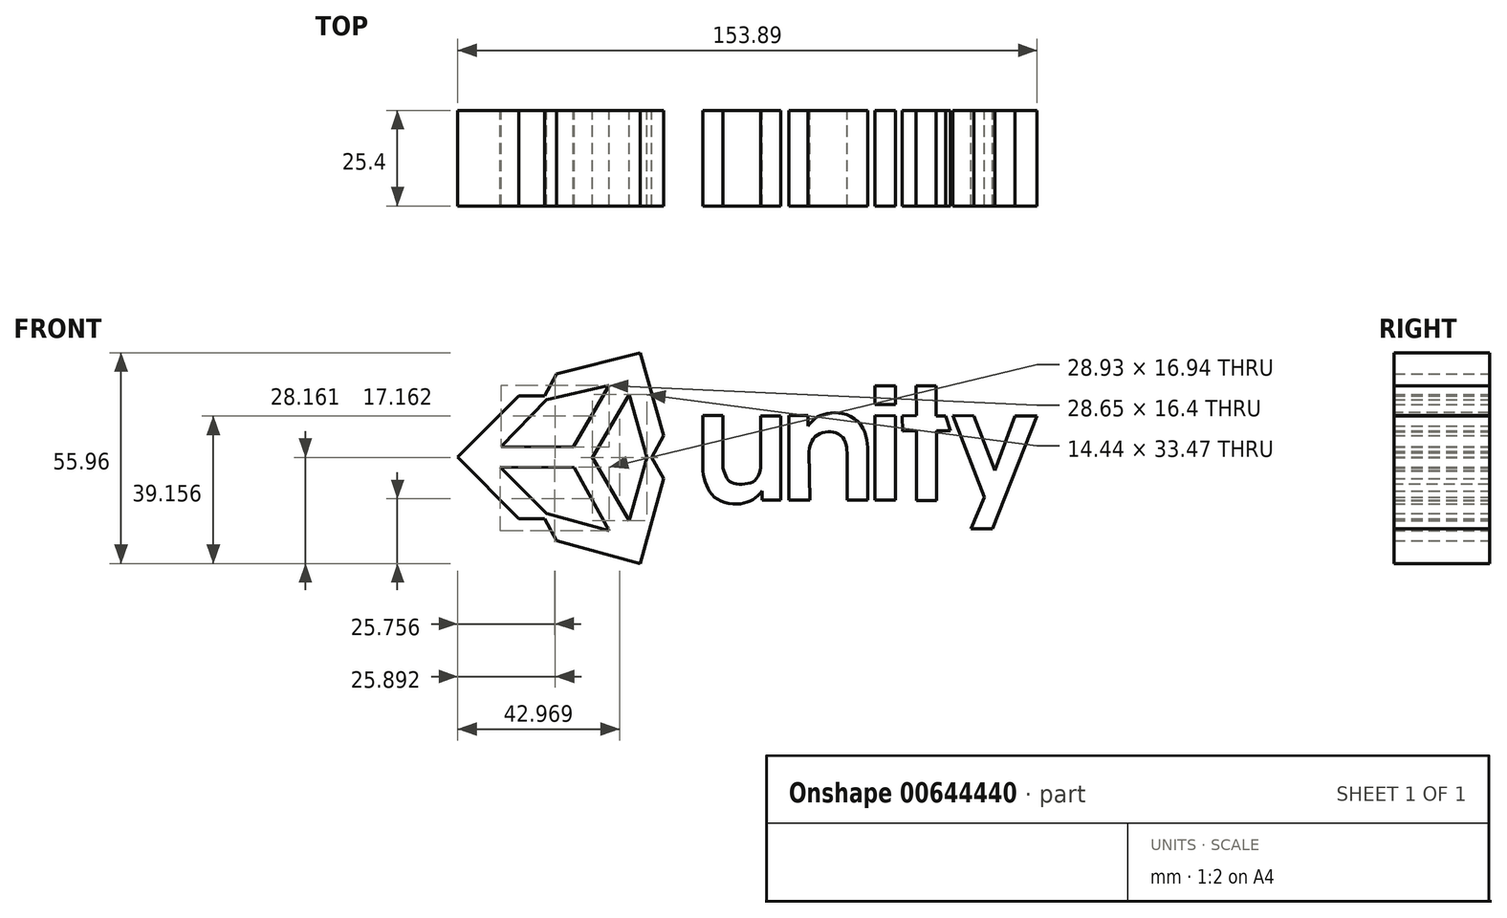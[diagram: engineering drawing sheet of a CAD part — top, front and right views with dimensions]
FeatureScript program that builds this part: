
annotation { "Feature Type Name" : "Feature", "Feature Type Description" : "" }
export const myFeature = defineFeature(function(context is Context, id is Id, definition is map)
    precondition{}
    {
        {
            var Q0;
            Q0=qCreatedBy(makeId("Front.planeOp"),FACE);
            var sketch = newSketch(context, id + "F0", { "sketchPlane" : qUnion([Q0])});
            skLineSegment(sketch, "E0", {"start": v(-78.08, -6.27) * mm, "end": v(-61.82, 10) * mm});
            skLineSegment(sketch, "E1", {"start": v(-61.82, 10) * mm, "end": v(-54.99, 10) * mm});
            skLineSegment(sketch, "E2", {"start": v(-54.99, 10) * mm, "end": v(-51.78, 15.87) * mm});
            skLineSegment(sketch, "E3", {"start": v(-51.78, 15.87) * mm, "end": v(-29.6, 21.48) * mm});
            skLineSegment(sketch, "E4", {"start": v(-29.6, 21.48) * mm, "end": v(-23.43, -0.5) * mm});
            skLineSegment(sketch, "E5", {"start": v(-23.43, -0.5) * mm, "end": v(-26.59, -6.29) * mm});
            skLineSegment(sketch, "E6", {"start": v(-26.59, -6.29) * mm, "end": v(-23.43, -11.97) * mm});
            skLineSegment(sketch, "E7", {"start": v(-23.43, -11.97) * mm, "end": v(-29.6, -34.48) * mm});
            skLineSegment(sketch, "E8", {"start": v(-29.6, -34.48) * mm, "end": v(-51.78, -28.4) * mm});
            skLineSegment(sketch, "E9", {"start": v(-51.78, -28.4) * mm, "end": v(-54.99, -22.58) * mm});
            skLineSegment(sketch, "E10", {"start": v(-54.99, -22.58) * mm, "end": v(-61.93, -22.58) * mm});
            skLineSegment(sketch, "E11", {"start": v(-61.93, -22.58) * mm, "end": v(-78.08, -6.27) * mm});
            skLineSegment(sketch, "E12", {"start": v(-66.79, -8.85) * mm, "end": v(-54.55, -21.2) * mm});
            skLineSegment(sketch, "E13", {"start": v(-54.55, -21.2) * mm, "end": v(-37.86, -25.79) * mm});
            skLineSegment(sketch, "E14", {"start": v(-37.86, -25.79) * mm, "end": v(-47.13, -9) * mm});
            skLineSegment(sketch, "E15", {"start": v(-47.13, -9) * mm, "end": v(-66.79, -8.85) * mm});
            skLineSegment(sketch, "E16", {"start": v(-54.55, 9.05) * mm, "end": v(-66.51, -3.38) * mm});
            skLineSegment(sketch, "E17", {"start": v(-66.51, -3.38) * mm, "end": v(-47.39, -3.52) * mm});
            skLineSegment(sketch, "E18", {"start": v(-47.39, -3.52) * mm, "end": v(-37.86, 12.88) * mm});
            skLineSegment(sketch, "E19", {"start": v(-37.86, 12.88) * mm, "end": v(-54.55, 9.05) * mm});
            skLineSegment(sketch, "E20", {"start": v(-42.33, -6.29) * mm, "end": v(-32.5, -23.06) * mm});
            skLineSegment(sketch, "E21", {"start": v(-32.5, -23.06) * mm, "end": v(-27.9, -6.29) * mm});
            skLineSegment(sketch, "E22", {"start": v(-27.9, -6.29) * mm, "end": v(-32.5, 10.42) * mm});
            skLineSegment(sketch, "E23", {"start": v(-32.5, 10.42) * mm, "end": v(-42.33, -6.29) * mm});
            skLineSegment(sketch, "E24", {"start": v(-12.94, 4.77) * mm, "end": v(-12.94, -9.9) * mm});
            skLineSegment(sketch, "E25", {"start": v(-12.94, 4.77) * mm, "end": v(-7.58, 4.77) * mm});
            skLineSegment(sketch, "E26", {"start": v(-7.58, 4.77) * mm, "end": v(-7.58, -9.16) * mm});
            skLineSegment(sketch, "E27", {"start": v(2.4, -8.68) * mm, "end": v(2.4, 4.73) * mm});
            skLineSegment(sketch, "E28", {"start": v(2.4, 4.73) * mm, "end": v(7.76, 4.73) * mm});
            skLineSegment(sketch, "E29", {"start": v(7.76, 4.73) * mm, "end": v(7.76, -17.67) * mm});
            skLineSegment(sketch, "E30", {"start": v(7.76, -17.67) * mm, "end": v(2.75, -17.67) * mm});
            skLineSegment(sketch, "E31", {"start": v(2.75, -17.67) * mm, "end": v(2.75, -15.25) * mm});
            skLineSegment(sketch, "E32", {"start": v(14.94, 2.03) * mm, "end": v(14.94, 4.78) * mm});
            skLineSegment(sketch, "E33", {"start": v(14.94, 4.78) * mm, "end": v(9.91, 4.78) * mm});
            skLineSegment(sketch, "E34", {"start": v(9.91, 4.78) * mm, "end": v(9.91, -17.64) * mm});
            skLineSegment(sketch, "E35", {"start": v(9.91, -17.64) * mm, "end": v(15.46, -17.64) * mm});
            skLineSegment(sketch, "E36", {"start": v(15.22, -4.63) * mm, "end": v(15.46, -17.64) * mm});
            skLineSegment(sketch, "E37", {"start": v(25.34, -5.04) * mm, "end": v(25.34, -17.64) * mm});
            skLineSegment(sketch, "E38", {"start": v(25.34, -17.64) * mm, "end": v(30.8, -17.64) * mm});
            skLineSegment(sketch, "E39", {"start": v(30.8, -17.64) * mm, "end": v(30.8, -4.77) * mm});
            skLineSegment(sketch, "E40", {"start": v(32.8, 4.8) * mm, "end": v(32.8, -17.61) * mm});
            skLineSegment(sketch, "E41", {"start": v(32.8, -17.61) * mm, "end": v(38.16, -17.61) * mm});
            skLineSegment(sketch, "E42", {"start": v(38.16, -17.61) * mm, "end": v(38.16, 4.73) * mm});
            skLineSegment(sketch, "E43", {"start": v(38.16, 4.73) * mm, "end": v(32.8, 4.8) * mm});
            skLineSegment(sketch, "E44", {"start": v(32.8, 12.66) * mm, "end": v(32.8, 7.78) * mm});
            skLineSegment(sketch, "E45", {"start": v(32.8, 7.78) * mm, "end": v(38.17, 7.78) * mm});
            skLineSegment(sketch, "E46", {"start": v(38.17, 7.78) * mm, "end": v(38.17, 12.66) * mm});
            skLineSegment(sketch, "E47", {"start": v(38.17, 12.66) * mm, "end": v(32.8, 12.66) * mm});
            skLineSegment(sketch, "E48", {"start": v(43.7, 12.66) * mm, "end": v(43.84, 4.8) * mm});
            skLineSegment(sketch, "E49", {"start": v(43.84, 4.8) * mm, "end": v(40, 4.73) * mm});
            skLineSegment(sketch, "E50", {"start": v(40, 4.73) * mm, "end": v(40.08, 0.7) * mm});
            skLineSegment(sketch, "E51", {"start": v(40.08, 0.7) * mm, "end": v(43.83, 0.77) * mm});
            skLineSegment(sketch, "E52", {"start": v(43.83, 0.77) * mm, "end": v(43.83, -17.74) * mm});
            skLineSegment(sketch, "E53", {"start": v(43.83, -17.74) * mm, "end": v(49.16, -17.74) * mm});
            skLineSegment(sketch, "E54", {"start": v(49.16, -17.74) * mm, "end": v(49.16, 0.77) * mm});
            skLineSegment(sketch, "E55", {"start": v(49.16, 0.77) * mm, "end": v(52.85, 0.77) * mm});
            skLineSegment(sketch, "E56", {"start": v(52.85, 0.77) * mm, "end": v(51.48, 4.67) * mm});
            skLineSegment(sketch, "E57", {"start": v(51.48, 4.67) * mm, "end": v(49.02, 4.67) * mm});
            skLineSegment(sketch, "E58", {"start": v(49.02, 4.67) * mm, "end": v(49.02, 12.68) * mm});
            skLineSegment(sketch, "E59", {"start": v(49.02, 12.68) * mm, "end": v(43.7, 12.66) * mm});
            skLineSegment(sketch, "E60", {"start": v(53.4, 4.83) * mm, "end": v(61.8, -16.86) * mm});
            skLineSegment(sketch, "E61", {"start": v(61.8, -16.86) * mm, "end": v(58.21, -25.3) * mm});
            skLineSegment(sketch, "E62", {"start": v(58.21, -25.3) * mm, "end": v(64, -25.27) * mm});
            skLineSegment(sketch, "E63", {"start": v(64, -25.27) * mm, "end": v(75.81, 4.73) * mm});
            skLineSegment(sketch, "E64", {"start": v(75.81, 4.73) * mm, "end": v(70.02, 4.71) * mm});
            skLineSegment(sketch, "E65", {"start": v(70.02, 4.71) * mm, "end": v(64.64, -9.8) * mm});
            skLineSegment(sketch, "E66", {"start": v(64.64, -9.8) * mm, "end": v(59.06, 4.73) * mm});
            skLineSegment(sketch, "E67", {"start": v(59.06, 4.73) * mm, "end": v(53.4, 4.83) * mm});
            skFitSpline(sketch, "E68", {"points": [v(-7.58, -9.16) * mm, v(-6.3, -12.2) * mm, v(-4, -13.35) * mm, v(0, -12.93) * mm, v(1.9, -10.93) * mm, v(2.4, -8.68) * mm], "startDerivative": vector(4.25, -15.78) * mm, "endDerivative": vector(0, 7.44) * mm});
            skFitSpline(sketch, "E69", {"points": [v(-12.94, -9.9) * mm, v(-12, -13.8) * mm, v(-10, -16.74) * mm, v(-6, -18.52) * mm, v(-1.88, -18.41) * mm, v(0.86, -17.15) * mm, v(2.75, -15.25) * mm], "startDerivative": vector(2.04, -24.47) * mm, "endDerivative": vector(12.32, 14.15) * mm});
            skFitSpline(sketch, "E70", {"points": [v(14.94, 2.03) * mm, v(16.9, 4.05) * mm, v(19.73, 5.27) * mm, v(23.72, 5.44) * mm, v(28.02, 3.4) * mm, v(30.38, -0.65) * mm, v(30.8, -4.77) * mm], "startDerivative": vector(12.62, 15.54) * mm, "endDerivative": vector(0.48, -23.78) * mm});
            skFitSpline(sketch, "E71", {"points": [v(15.22, -4.63) * mm, v(15.75, -2.53) * mm, v(17.13, -0.58) * mm, v(19.5, 0.4) * mm, v(21.77, 0.4) * mm, v(23.96, -0.82) * mm, v(25.1, -2.93) * mm, v(25.34, -5.04) * mm], "startDerivative": vector(2.77, 15.37) * mm, "endDerivative": vector(0.64, -15.43) * mm});
            skSolve(sketch);
        }
        {
            var Q0;
            Q0=makeQuery(id+"F0.imprint","IMPRINT",FACE,{"disambiguationData":[TD([[makeQuery(id+"F0.imprint","IMPRINT",EDGE,{"derivedFrom":sQuery(id+"F0.wireOp",EDGE,"E0")}),-1.0]])]});
            var Q1;
            Q1=makeQuery(id+"F0.imprint","IMPRINT",FACE,{"disambiguationData":[TD([[makeQuery(id+"F0.imprint","IMPRINT",EDGE,{"derivedFrom":sQuery(id+"F0.wireOp",EDGE,"E24")}),1.0]])]});
            var Q2;
            Q2=makeQuery(id+"F0.imprint","IMPRINT",FACE,{"disambiguationData":[TD([[makeQuery(id+"F0.imprint","IMPRINT",EDGE,{"derivedFrom":sQuery(id+"F0.wireOp",EDGE,"E32")}),1.0]])]});
            var Q3;
            Q3=makeQuery(id+"F0.imprint","IMPRINT",FACE,{"disambiguationData":[TD([[makeQuery(id+"F0.imprint","IMPRINT",EDGE,{"derivedFrom":sQuery(id+"F0.wireOp",EDGE,"E40")}),1.0]])]});
            var Q4;
            Q4=makeQuery(id+"F0.imprint","IMPRINT",FACE,{"disambiguationData":[TD([[makeQuery(id+"F0.imprint","IMPRINT",EDGE,{"derivedFrom":sQuery(id+"F0.wireOp",EDGE,"E44")}),1.0]])]});
            var Q5;
            Q5=makeQuery(id+"F0.imprint","IMPRINT",FACE,{"disambiguationData":[TD([[makeQuery(id+"F0.imprint","IMPRINT",EDGE,{"derivedFrom":sQuery(id+"F0.wireOp",EDGE,"E48")}),1.0]])]});
            var Q6;
            Q6=makeQuery(id+"F0.imprint","IMPRINT",FACE,{"disambiguationData":[TD([[makeQuery(id+"F0.imprint","IMPRINT",EDGE,{"derivedFrom":sQuery(id+"F0.wireOp",EDGE,"E60")}),1.0]])]});
            extrude(context, id + "F1", {"entities" : qUnion([Q0, Q1, Q2, Q3, Q4, Q5, Q6]), "depth" : 25.4 * mm, "offsetDistance" : 25.4 * mm});
        }
    });
